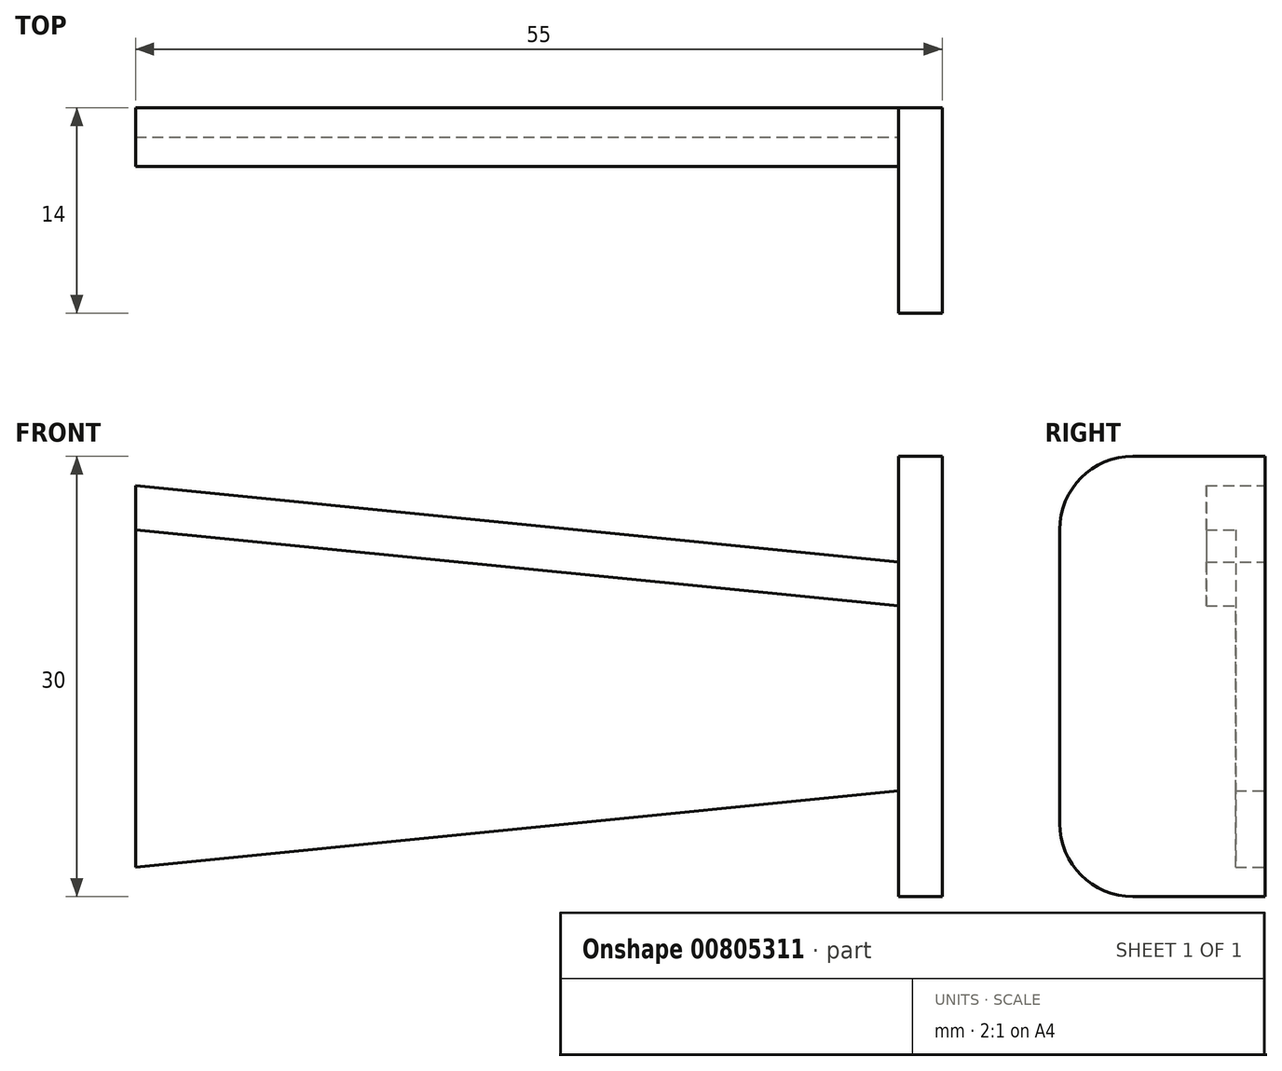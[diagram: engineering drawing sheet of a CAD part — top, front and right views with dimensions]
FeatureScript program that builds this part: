
annotation { "Feature Type Name" : "Feature", "Feature Type Description" : "" }
export const myFeature = defineFeature(function(context is Context, id is Id, definition is map)
    precondition{}
    {
        {
            var Q0;
            Q0=qCreatedBy(makeId("Front.planeOp"),FACE);
            var sketch = newSketch(context, id + "F0", { "sketchPlane" : qUnion([Q0])});
            skLineSegment(sketch, "E0", {"start": v(-25.1, 0) * mm, "end": v(26.9, 0) * mm});
            skLineSegment(sketch, "E1", {"start": v(-25.1, 0) * mm, "end": v(-25.1, -13) * mm});
            skLineSegment(sketch, "E2", {"start": v(-25.1, -13) * mm, "end": v(26.9, -7.8) * mm});
            skLineSegment(sketch, "E3.MirrorCS", {"start": v(-25.1, 0) * mm, "end": v(-25.1, 13) * mm});
            skLineSegment(sketch, "E4.MirrorCS", {"start": v(-25.1, 13) * mm, "end": v(26.9, 7.8) * mm});
            skLineSegment(sketch, "E5", {"start": v(26.9, -7.8) * mm, "end": v(26.9, 7.8) * mm});
            skLineSegment(sketch, "E6", {"start": v(-25.1, 10) * mm, "end": v(26.9, 4.8) * mm});
            skLineSegment(sketch, "E7", {"start": v(26.9, 0) * mm, "end": v(26.9, 15) * mm});
            skLineSegment(sketch, "E8", {"start": v(26.9, 15) * mm, "end": v(29.9, 15) * mm});
            skLineSegment(sketch, "E9.MirrorCS", {"start": v(26.9, 0) * mm, "end": v(26.9, -15) * mm});
            skLineSegment(sketch, "E10", {"start": v(26.9, -15) * mm, "end": v(29.9, -15) * mm});
            skLineSegment(sketch, "E11", {"start": v(29.9, 15) * mm, "end": v(29.9, -15) * mm});
            skLineSegment(sketch, "E12", {"start": v(26.9, 0) * mm, "end": v(29.9, 0) * mm});
            skSolve(sketch);
        }
        {
            var Q0;
            {var subQ0=sQuery(id+"F0.wireOp",EDGE,"E0");Q0=makeQuery(id+"F0.imprint","IMPRINT",FACE,{"disambiguationData":[TD([[makeQuery(id+"F0.imprint","IMPRINT",EDGE,{"derivedFrom":subQ0}),-1.0]])]});}
            var Q1;
            {var subQ0=sQuery(id+"F0.wireOp",EDGE,"E0");Q1=makeQuery(id+"F0.imprint","IMPRINT",FACE,{"disambiguationData":[TD([[makeQuery(id+"F0.imprint","IMPRINT",EDGE,{"derivedFrom":subQ0}),1.0]])]});}
            extrude(context, id + "F1", {"entities" : qUnion([Q0, Q1]), "depth" : 2 * mm, "offsetDistance" : 25 * mm});
        }
        {
            var Q0;
            {var subQ0=sQuery(id+"F0.wireOp",EDGE,"E8");Q0=makeQuery(id+"F0.imprint","IMPRINT",FACE,{"disambiguationData":[TD([[makeQuery(id+"F0.imprint","IMPRINT",EDGE,{"derivedFrom":subQ0}),-1.0]])]});}
            extrude(context, id + "F2", {"entities" : qUnion([Q0]), "operationType" : NewBodyOperationType.ADD, "depth" : 14 * mm, "offsetDistance" : 25 * mm});
        }
        {
            var Q0;
            {var subQ0=sQuery(id+"F0.wireOp",EDGE,"E4.MirrorCS");Q0=makeQuery(id+"F0.imprint","IMPRINT",FACE,{"disambiguationData":[TD([[makeQuery(id+"F0.imprint","IMPRINT",EDGE,{"derivedFrom":subQ0}),-1.0]])]});}
            extrude(context, id + "F3", {"entities" : qUnion([Q0]), "operationType" : NewBodyOperationType.ADD, "depth" : 4 * mm, "offsetDistance" : 25 * mm});
        }
        {
            var Q0;
            {var subQ1=sQuery(id+"F0.wireOp",EDGE,"E10");Q0=makeQuery(id+"F0.imprint","IMPRINT",FACE,{"disambiguationData":[TD([[makeQuery(id+"F0.imprint","IMPRINT",EDGE,{"derivedFrom":subQ1}),1.0]])]});}
            extrude(context, id + "F4", {"entities" : qUnion([Q0]), "operationType" : NewBodyOperationType.ADD, "depth" : 14 * mm, "offsetDistance" : 25 * mm});
        }
        {
            var Q0;
            Q0=makeQuery(id+"F4.opExtrude","CAP_EDGE",EDGE,{"disambiguationData":[OSD([sQuery(id+"F0.wireOp",EDGE,"E10")])],"isStart":false});
            var Q1;
            Q1=makeQuery(id+"F2.opExtrude","CAP_EDGE",EDGE,{"disambiguationData":[OSD([sQuery(id+"F0.wireOp",EDGE,"E8")])],"isStart":false});
            fillet(context, id + "F5", {"entities" : qUnion([Q0, Q1]), "radius" : 5 * mm, "tangentPropagation" : true, "allowEdgeOverflow" : false});
        }
    });
